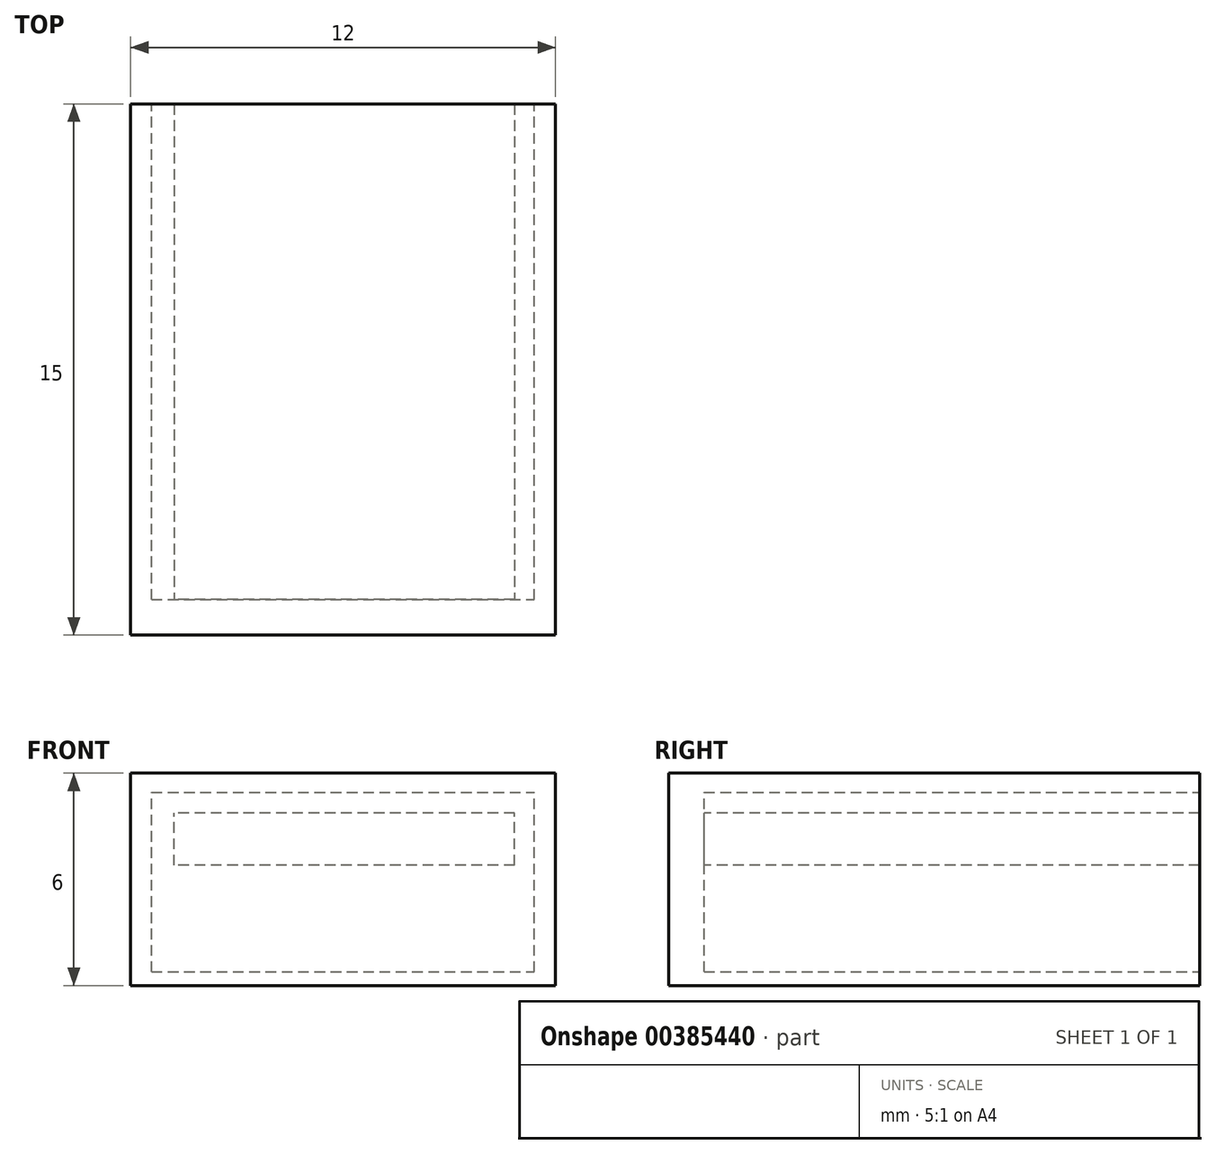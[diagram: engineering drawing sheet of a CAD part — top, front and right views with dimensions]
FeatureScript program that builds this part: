
annotation { "Feature Type Name" : "Feature", "Feature Type Description" : "" }
export const myFeature = defineFeature(function(context is Context, id is Id, definition is map)
    precondition{}
    {
        {
            var Q0;
            Q0=qCreatedBy(makeId("Top.planeOp"),FACE);
            var sketch = newSketch(context, id + "F0", { "sketchPlane" : qUnion([Q0])});
            skLineSegment(sketch, "E0.bottom", {"start": v(6, -7.5) * mm, "end": v(-6, -7.5) * mm});
            skLineSegment(sketch, "E0.top", {"start": v(6, 7.5) * mm, "end": v(-6, 7.5) * mm});
            skLineSegment(sketch, "E0.left", {"start": v(6, -7.5) * mm, "end": v(6, 7.5) * mm});
            skLineSegment(sketch, "E0.right", {"start": v(-6, -7.5) * mm, "end": v(-6, 7.5) * mm});
            skPoint(sketch, "E0.middle", {"position": v(0, 0) * mm});
            skSolve(sketch);
        }
        {
            var Q0;
            Q0=makeQuery(id+"F0.imprint","IMPRINT",FACE,{"disambiguationData":[TD([[makeQuery(id+"F0.imprint","IMPRINT",EDGE,{"derivedFrom":sQuery(id+"F0.wireOp",EDGE,"E0.bottom")}),-1.0]])]});
            extrude(context, id + "F1", {"entities" : qUnion([Q0]), "depth" : 6 * mm});
        }
        {
            var Q0;
            Q0=makeQuery(id+"F1.opExtrude","SWEPT_FACE",FACE,{"disambiguationData":[OSD([sQuery(id+"F0.wireOp",EDGE,"E0.top")])]});
            var sketch = newSketch(context, id + "F2", { "sketchPlane" : qUnion([Q0])});
            skLineSegment(sketch, "E1.bottom", {"start": v(5.4, 0.38) * mm, "end": v(-5.4, 0.38) * mm});
            skLineSegment(sketch, "E1.top", {"start": v(5.4, 5.46) * mm, "end": v(-5.4, 5.46) * mm});
            skLineSegment(sketch, "E1.left", {"start": v(5.4, 0.38) * mm, "end": v(5.4, 5.46) * mm});
            skLineSegment(sketch, "E1.right", {"start": v(-5.4, 0.38) * mm, "end": v(-5.4, 5.46) * mm});
            skPoint(sketch, "E1.middle", {"position": v(0, 2.92) * mm});
            skPoint(sketch, "E2", {"position": v(0, 6) * mm});
            skSolve(sketch);
        }
        {
            var Q0;
            Q0=qSketchRegion(id+"F2",true);
            extrude(context, id + "F3", {"entities" : qUnion([Q0]), "operationType" : NewBodyOperationType.REMOVE, "oppositeDirection" : true, "depth" : 14 * mm});
        }
        {
            var Q0;
            Q0=makeQuery(id+"F3.boolean.opBoolean","COPY",FACE,{"derivedFrom":makeQuery(id+"F3.opExtrude","CAP_FACE",FACE,{"disambiguationData":[OSD([sQuery(id+"F2.wireOp",EDGE,"E1.bottom"),sQuery(id+"F2.wireOp",EDGE,"E1.top"),sQuery(id+"F2.wireOp",EDGE,"E1.left"),sQuery(id+"F2.wireOp",EDGE,"E1.right")])],"isStart":false})});
            var sketch = newSketch(context, id + "F4", { "sketchPlane" : qUnion([Q0])});
            skLineSegment(sketch, "E3.bottom", {"start": v(-4.85, 3.4) * mm, "end": v(4.77, 3.4) * mm});
            skLineSegment(sketch, "E3.top", {"start": v(-4.85, 4.87) * mm, "end": v(4.77, 4.87) * mm});
            skLineSegment(sketch, "E3.left", {"start": v(-4.85, 3.4) * mm, "end": v(-4.85, 4.87) * mm});
            skLineSegment(sketch, "E3.right", {"start": v(4.77, 3.4) * mm, "end": v(4.77, 4.87) * mm});
            skSolve(sketch);
        }
        {
            var Q0;
            Q0=makeQuery(id+"F4.imprint","IMPRINT",FACE,{"disambiguationData":[TD([[makeQuery(id+"F4.imprint","IMPRINT",EDGE,{"derivedFrom":sQuery(id+"F4.wireOp",EDGE,"E3.bottom")}),1.0]])]});
            extrude(context, id + "F5", {"entities" : qUnion([Q0]), "operationType" : NewBodyOperationType.ADD, "depth" : 14 * mm});
        }
    });
